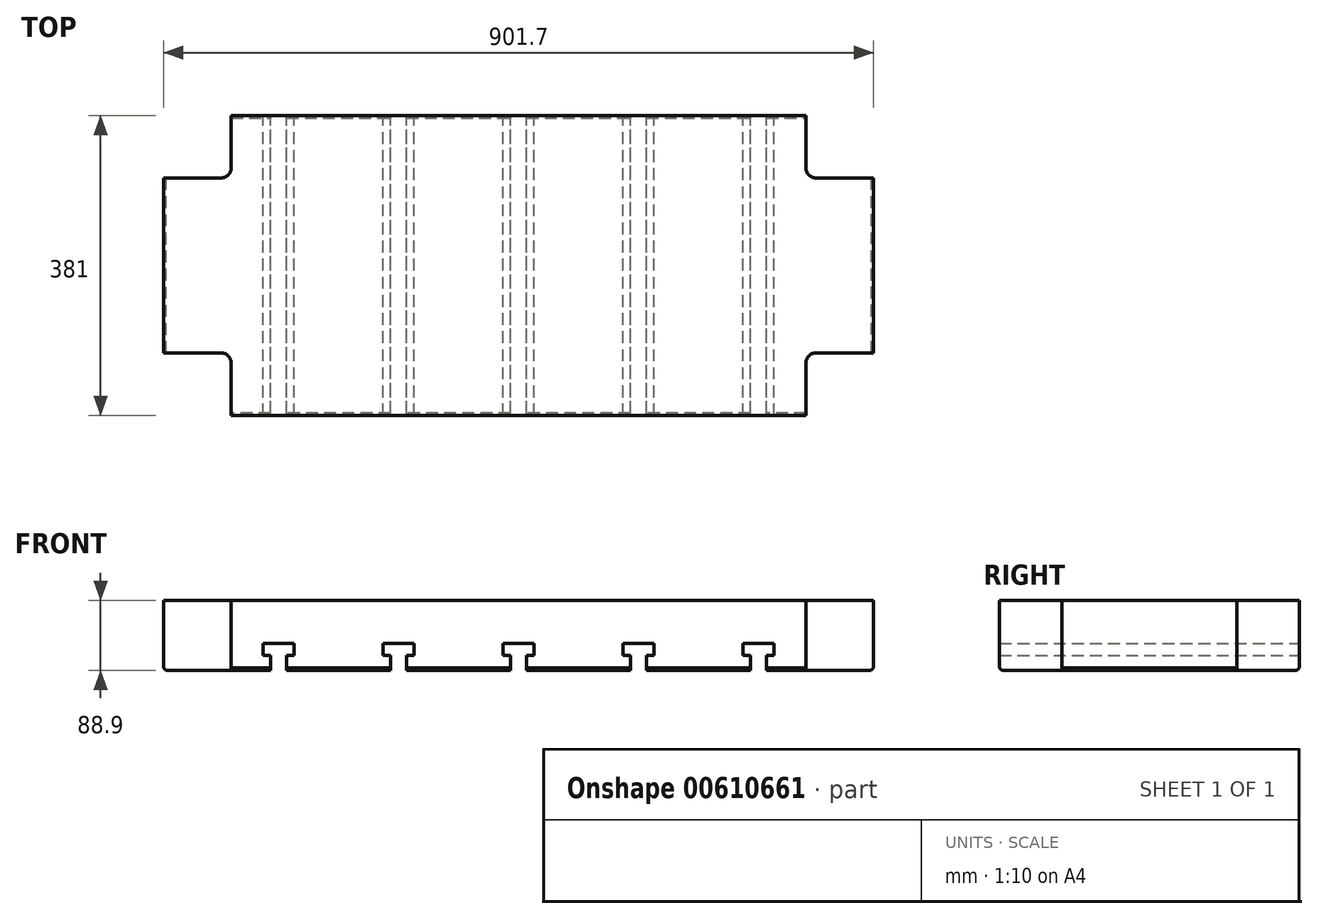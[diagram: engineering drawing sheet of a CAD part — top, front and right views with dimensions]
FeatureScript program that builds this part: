
annotation { "Feature Type Name" : "Feature", "Feature Type Description" : "" }
export const myFeature = defineFeature(function(context is Context, id is Id, definition is map)
    precondition{}
    {
        {
            var Q0;
            Q0=qCreatedBy(makeId("Top.planeOp"),FACE);
            var sketch = newSketch(context, id + "F0", { "sketchPlane" : qUnion([Q0])});
            skLineSegment(sketch, "E0.bottom", {"start": v(450.85, -190.5) * mm, "end": v(-450.85, -190.5) * mm});
            skLineSegment(sketch, "E0.top", {"start": v(450.85, 190.5) * mm, "end": v(-450.85, 190.5) * mm});
            skLineSegment(sketch, "E0.left", {"start": v(450.85, -190.5) * mm, "end": v(450.85, 190.5) * mm});
            skLineSegment(sketch, "E0.right", {"start": v(-450.85, -190.5) * mm, "end": v(-450.85, 190.5) * mm});
            skPoint(sketch, "E0.middle", {"position": v(0, 0) * mm});
            skSolve(sketch);
        }
        {
            var Q0;
            Q0=qSketchRegion(id+"F0",true);
            extrude(context, id + "F1", {"entities" : qUnion([Q0]), "depth" : 88.9 * mm, "offsetDistance" : 25.4 * mm});
        }
        {
            var Q0;
            Q0=makeQuery(id+"F1.opExtrude","CAP_FACE",FACE,{"disambiguationData":[OSD([sQuery(id+"F0.wireOp",EDGE,"E0.bottom"),sQuery(id+"F0.wireOp",EDGE,"E0.top"),sQuery(id+"F0.wireOp",EDGE,"E0.left"),sQuery(id+"F0.wireOp",EDGE,"E0.right")])],"isStart":false});
            chamfer(context, id + "F2", {"entities" : qUnion([Q0]), "width" : 3.17 * mm, "tangentPropagation" : true});
        }
        {
            var Q0;
            Q0=makeQuery(id+"F1.opExtrude","SWEPT_FACE",FACE,{"disambiguationData":[OSD([sQuery(id+"F0.wireOp",EDGE,"E0.bottom")])]});
            var sketch = newSketch(context, id + "F3", { "sketchPlane" : qUnion([Q0])});
            skLineSegment(sketch, "E1.0", {"start": v(-447.68, 88.9) * mm, "end": v(447.68, 88.9) * mm});
            skLineSegment(sketch, "E2", {"start": v(-10.32, 88.9) * mm, "end": v(-10.32, 69.85) * mm});
            skLineSegment(sketch, "E3", {"start": v(-10.32, 69.85) * mm, "end": v(-19.84, 69.85) * mm});
            skLineSegment(sketch, "E4", {"start": v(-19.84, 69.85) * mm, "end": v(-19.84, 54.77) * mm});
            skLineSegment(sketch, "E5", {"start": v(-19.84, 54.77) * mm, "end": v(19.84, 54.77) * mm});
            skLineSegment(sketch, "E6", {"start": v(19.84, 54.77) * mm, "end": v(19.84, 69.85) * mm});
            skLineSegment(sketch, "E7", {"start": v(19.84, 69.85) * mm, "end": v(10.32, 69.85) * mm});
            skLineSegment(sketch, "E8", {"start": v(10.32, 69.85) * mm, "end": v(10.32, 88.9) * mm});
            skLineSegment(sketch, "E9.1.0.0", {"start": v(172.24, 54.77) * mm, "end": v(172.24, 69.85) * mm});
            skLineSegment(sketch, "E9.1.0.1", {"start": v(132.56, 54.77) * mm, "end": v(172.24, 54.77) * mm});
            skLineSegment(sketch, "E9.1.0.2", {"start": v(162.72, 69.85) * mm, "end": v(162.72, 88.9) * mm});
            skLineSegment(sketch, "E9.1.0.3", {"start": v(132.56, 69.85) * mm, "end": v(132.56, 54.77) * mm});
            skLineSegment(sketch, "E9.1.0.4", {"start": v(142.08, 88.9) * mm, "end": v(142.08, 69.85) * mm});
            skLineSegment(sketch, "E9.1.0.5", {"start": v(172.24, 69.85) * mm, "end": v(162.72, 69.85) * mm});
            skLineSegment(sketch, "E9.1.0.6", {"start": v(142.08, 69.85) * mm, "end": v(132.56, 69.85) * mm});
            skLineSegment(sketch, "E9.2.0.0", {"start": v(324.64, 54.77) * mm, "end": v(324.64, 69.85) * mm});
            skLineSegment(sketch, "E9.2.0.1", {"start": v(284.96, 54.77) * mm, "end": v(324.64, 54.77) * mm});
            skLineSegment(sketch, "E9.2.0.2", {"start": v(315.12, 69.85) * mm, "end": v(315.12, 88.9) * mm});
            skLineSegment(sketch, "E9.2.0.3", {"start": v(284.96, 69.85) * mm, "end": v(284.96, 54.77) * mm});
            skLineSegment(sketch, "E9.2.0.4", {"start": v(294.48, 88.9) * mm, "end": v(294.48, 69.85) * mm});
            skLineSegment(sketch, "E9.2.0.5", {"start": v(324.64, 69.85) * mm, "end": v(315.12, 69.85) * mm});
            skLineSegment(sketch, "E9.2.0.6", {"start": v(294.48, 69.85) * mm, "end": v(284.96, 69.85) * mm});
            skLineSegment(sketch, "E9.direction1", {"start": v(-19.84, 54.77) * mm, "end": v(132.56, 54.77) * mm, "construction": true});
            skLineSegment(sketch, "E10.1.0.0", {"start": v(-172.24, 69.85) * mm, "end": v(-172.24, 54.77) * mm});
            skLineSegment(sketch, "E10.1.0.1", {"start": v(-162.72, 88.9) * mm, "end": v(-162.72, 69.85) * mm});
            skLineSegment(sketch, "E10.1.0.2", {"start": v(-172.24, 54.77) * mm, "end": v(-132.56, 54.77) * mm});
            skLineSegment(sketch, "E10.1.0.3", {"start": v(-132.56, 54.77) * mm, "end": v(-132.56, 69.85) * mm});
            skLineSegment(sketch, "E10.1.0.4", {"start": v(-142.08, 69.85) * mm, "end": v(-142.08, 88.9) * mm});
            skLineSegment(sketch, "E10.1.0.5", {"start": v(-162.72, 69.85) * mm, "end": v(-172.24, 69.85) * mm});
            skLineSegment(sketch, "E10.1.0.6", {"start": v(-132.56, 69.85) * mm, "end": v(-142.08, 69.85) * mm});
            skLineSegment(sketch, "E10.2.0.0", {"start": v(-324.64, 69.85) * mm, "end": v(-324.64, 54.77) * mm});
            skLineSegment(sketch, "E10.2.0.1", {"start": v(-315.12, 88.9) * mm, "end": v(-315.12, 69.85) * mm});
            skLineSegment(sketch, "E10.2.0.2", {"start": v(-324.64, 54.77) * mm, "end": v(-284.96, 54.77) * mm});
            skLineSegment(sketch, "E10.2.0.3", {"start": v(-284.96, 54.77) * mm, "end": v(-284.96, 69.85) * mm});
            skLineSegment(sketch, "E10.2.0.4", {"start": v(-294.48, 69.85) * mm, "end": v(-294.48, 88.9) * mm});
            skLineSegment(sketch, "E10.2.0.5", {"start": v(-315.12, 69.85) * mm, "end": v(-324.64, 69.85) * mm});
            skLineSegment(sketch, "E10.2.0.6", {"start": v(-284.96, 69.85) * mm, "end": v(-294.48, 69.85) * mm});
            skLineSegment(sketch, "E10.direction1", {"start": v(-19.84, 54.77) * mm, "end": v(-172.24, 54.77) * mm, "construction": true});
            skSolve(sketch);
        }
        {
            var Q0;
            Q0=qSketchRegion(id+"F3",true);
            extrude(context, id + "F4", {"entities" : qUnion([Q0]), "operationType" : NewBodyOperationType.REMOVE, "endBound" : BoundingType.THROUGH_ALL, "oppositeDirection" : true, "depth" : 25.4 * mm, "offsetDistance" : 25.4 * mm});
        }
        {
            var Q0;
            Q0=makeQuery(id+"F1.opExtrude","CAP_FACE",FACE,{"disambiguationData":[OSD([sQuery(id+"F0.wireOp",EDGE,"E0.bottom"),sQuery(id+"F0.wireOp",EDGE,"E0.top"),sQuery(id+"F0.wireOp",EDGE,"E0.left"),sQuery(id+"F0.wireOp",EDGE,"E0.right")])],"isStart":true});
            var sketch = newSketch(context, id + "F5", { "sketchPlane" : qUnion([Q0])});
            skLineSegment(sketch, "E11", {"start": v(-365.12, -190.5) * mm, "end": v(-365.12, -123.83) * mm});
            skLineSegment(sketch, "E12", {"start": v(-377.82, -111.13) * mm, "end": v(-450.85, -111.13) * mm});
            skPoint(sketch, "E13.visualSharp", {"position": v(-365.12, -111.13) * mm});
            skArc(sketch, "E13.filletArc", {"start": v(-365.12, -123.83) * mm, "mid": v(-368.84, -114.84) * mm, "end": v(-377.82, -111.13) * mm});
            skArc(sketch, "E14.MirrorCS", {"start": v(365.12, -123.83) * mm, "mid": v(368.84, -114.84) * mm, "end": v(377.82, -111.13) * mm});
            skPoint(sketch, "E15.MirrorP", {"position": v(365.12, -111.13) * mm});
            skLineSegment(sketch, "E16.MirrorCS", {"start": v(365.12, -190.5) * mm, "end": v(365.12, -123.83) * mm});
            skLineSegment(sketch, "E17.MirrorCS", {"start": v(377.82, -111.13) * mm, "end": v(450.85, -111.13) * mm});
            skArc(sketch, "E18.MirrorCS", {"start": v(365.12, 123.83) * mm, "mid": v(368.84, 114.84) * mm, "end": v(377.82, 111.13) * mm});
            skArc(sketch, "E19.MirrorCS", {"start": v(-365.12, 123.83) * mm, "mid": v(-368.84, 114.84) * mm, "end": v(-377.82, 111.13) * mm});
            skLineSegment(sketch, "E20.MirrorCS", {"start": v(-377.82, 111.13) * mm, "end": v(-450.85, 111.13) * mm});
            skLineSegment(sketch, "E21.MirrorCS", {"start": v(-365.12, 190.5) * mm, "end": v(-365.12, 123.83) * mm});
            skPoint(sketch, "E22.MirrorP", {"position": v(365.12, 111.13) * mm});
            skLineSegment(sketch, "E23.MirrorCS", {"start": v(377.82, 111.13) * mm, "end": v(450.85, 111.13) * mm});
            skLineSegment(sketch, "E24.MirrorCS", {"start": v(365.12, 190.5) * mm, "end": v(365.12, 123.83) * mm});
            skPoint(sketch, "E25.MirrorP", {"position": v(-365.12, 111.13) * mm});
            skLineSegment(sketch, "E26", {"start": v(-450.85, -111.13) * mm, "end": v(-450.85, -190.5) * mm});
            skLineSegment(sketch, "E27", {"start": v(-450.85, -190.5) * mm, "end": v(-365.12, -190.5) * mm});
            skLineSegment(sketch, "E28", {"start": v(365.12, -190.5) * mm, "end": v(450.85, -190.5) * mm});
            skLineSegment(sketch, "E29", {"start": v(450.85, -190.5) * mm, "end": v(450.85, -111.13) * mm});
            skLineSegment(sketch, "E30", {"start": v(450.85, 111.13) * mm, "end": v(450.85, 190.5) * mm});
            skLineSegment(sketch, "E31", {"start": v(450.85, 190.5) * mm, "end": v(365.12, 190.5) * mm});
            skLineSegment(sketch, "E32", {"start": v(-365.12, 190.5) * mm, "end": v(-450.85, 190.5) * mm});
            skLineSegment(sketch, "E33", {"start": v(-450.85, 190.5) * mm, "end": v(-450.85, 111.13) * mm});
            skSolve(sketch);
        }
        {
            var Q0;
            Q0 = qSketchRegion(id + "F5", true);
            extrude(context, id + "F6", {"entities" : qUnion([Q0]), "operationType" : NewBodyOperationType.REMOVE, "endBound" : BoundingType.THROUGH_ALL, "oppositeDirection" : true, "depth" : 25.4 * mm, "offsetDistance" : 25.4 * mm});
        }
        {
            var Q0;
            Q0=makeQuery(id+"F1.opExtrude","CAP_FACE",FACE,{"disambiguationData":[OSD([sQuery(id+"F0.wireOp",EDGE,"E0.bottom"),sQuery(id+"F0.wireOp",EDGE,"E0.top"),sQuery(id+"F0.wireOp",EDGE,"E0.left"),sQuery(id+"F0.wireOp",EDGE,"E0.right")])],"isStart":true});
            var sketch = newSketch(context, id + "F7", { "sketchPlane" : qUnion([Q0])});
            skLineSegment(sketch, "E34", {"start": v(-102.03, 0) * mm, "end": v(104.14, 0) * mm, "construction": true});
            skSolve(sketch);
        }
        {
            var Q0;
            Q0=makeQuery(id+"F1.opExtrude","SWEPT_BODY",BODY,{"disambiguationData":[OSD([sQuery(id+"F0.wireOp",EDGE,"E0.bottom"),sQuery(id+"F0.wireOp",EDGE,"E0.top"),sQuery(id+"F0.wireOp",EDGE,"E0.left"),sQuery(id+"F0.wireOp",EDGE,"E0.right")])]});
            var Q1;
            Q1=sQuery(id+"F7.wireOp",EDGE,"E34");
            transform(context, id + "F8", {"entities" : qUnion([Q0]), "transformType" : TransformType.ROTATION, "transformAxis" : qUnion([Q1]), "angle" : 180 * degree, "makeCopy" : false});
        }
    });
